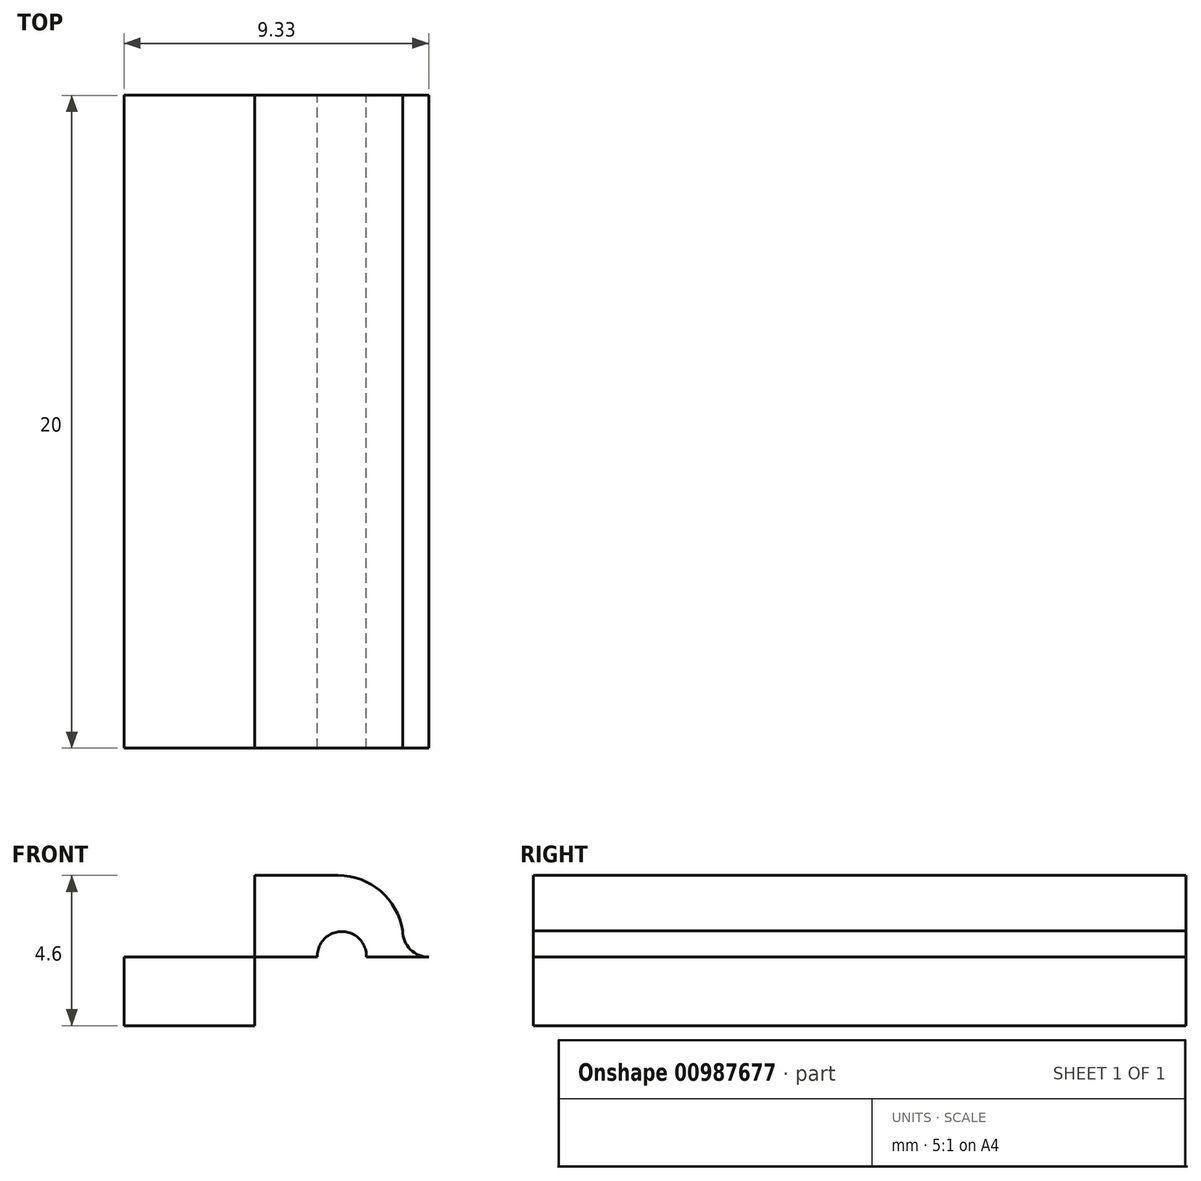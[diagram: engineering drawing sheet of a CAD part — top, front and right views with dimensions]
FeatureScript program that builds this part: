
annotation { "Feature Type Name" : "Feature", "Feature Type Description" : "" }
export const myFeature = defineFeature(function(context is Context, id is Id, definition is map)
    precondition{}
    {
        {
            var Q0;
            Q0=qCreatedBy(makeId("Top.planeOp"),FACE);
            var sketch = newSketch(context, id + "F0", { "sketchPlane" : qUnion([Q0])});
            skLineSegment(sketch, "E0", {"start": v(-65.72, -15.52) * mm, "end": v(10.28, -15.52) * mm});
            skLineSegment(sketch, "E1", {"start": v(-65.72, -15.52) * mm, "end": v(-65.72, 4.48) * mm});
            skLineSegment(sketch, "E2", {"start": v(-65.72, 4.48) * mm, "end": v(10.28, 4.48) * mm});
            skLineSegment(sketch, "E3", {"start": v(14.28, 0.48) * mm, "end": v(14.28, -11.52) * mm});
            skPoint(sketch, "E4.visualSharp", {"position": v(14.28, 4.48) * mm});
            skArc(sketch, "E4.filletArc", {"start": v(14.28, 0.48) * mm, "mid": v(13.1, 3.3) * mm, "end": v(10.28, 4.48) * mm});
            skPoint(sketch, "E5.visualSharp", {"position": v(14.28, -15.52) * mm});
            skArc(sketch, "E5.filletArc", {"start": v(10.28, -15.52) * mm, "mid": v(13.1, -14.35) * mm, "end": v(14.28, -11.52) * mm});
            skLineSegment(sketch, "E6", {"start": v(14.28, -5.52) * mm, "end": v(3.28, -5.52) * mm});
            skLineSegment(sketch, "E7", {"start": v(-65.72, 4.48) * mm, "end": v(-61.72, 4.48) * mm});
            skLineSegment(sketch, "E8", {"start": v(-61.72, 4.48) * mm, "end": v(-61.72, -15.52) * mm});
            skSolve(sketch);
        }
        {
            var Q0;
            Q0=makeQuery(id+"F0.imprint","IMPRINT",FACE,{"disambiguationData":[TD([[makeQuery(id+"F0.imprint","IMPRINT",EDGE,{"derivedFrom":sQuery(id+"F0.wireOp",EDGE,"E2")}),-1.0]])]});
            var Q1;
            Q1=makeQuery(id+"F0.imprint","IMPRINT",FACE,{"disambiguationData":[TD([[makeQuery(id+"F0.imprint","IMPRINT",EDGE,{"derivedFrom":sQuery(id+"F0.wireOp",EDGE,"6CRX7QyW-g7Fc-n8MB-8x00-72Ocf16J1GDi")}),-1.0]])]});
            extrude(context, id + "F1", {"entities" : qUnion([Q0, Q1]), "oppositeDirection" : true, "depth" : 2.1 * mm, "offsetDistance" : 25 * mm});
        }
        {
            var Q0;
            Q0=makeQuery(id+"F1.opExtrude","CAP_FACE",FACE,{"disambiguationData":[OSD([sQuery(id+"F0.wireOp",EDGE,"E0"),sQuery(id+"F0.wireOp",EDGE,"E2"),sQuery(id+"F0.wireOp",EDGE,"E3"),sQuery(id+"F0.wireOp",EDGE,"E4.filletArc"),sQuery(id+"F0.wireOp",EDGE,"E5.filletArc"),sQuery(id+"F0.wireOp",EDGE,"E8")])],"isStart":false});
            var sketch = newSketch(context, id + "F2", { "sketchPlane" : qUnion([Q0])});
            skLineSegment(sketch, "E9", {"start": v(14.28, 5.52) * mm, "end": v(3.28, 5.52) * mm});
            skCircle(sketch, "E10", {"center": v(3.28, 5.52) * mm, "radius": 1.5 * mm});
            skSolve(sketch);
        }
        {
            var Q0;
            Q0=makeQuery(id+"F2.imprint","IMPRINT",FACE,{"disambiguationData":[TD([[makeQuery(id+"F2.imprint","IMPRINT",EDGE,{"derivedFrom":sQuery(id+"F2.wireOp",EDGE,"E10")}),1.0]])]});
            extrude(context, id + "F3", {"entities" : qUnion([Q0]), "operationType" : NewBodyOperationType.REMOVE, "endBound" : BoundingType.THROUGH_ALL, "oppositeDirection" : true, "depth" : 25 * mm, "offsetDistance" : 25 * mm});
        }
        {
            var Q0;
            Q0=makeQuery(id+"F0.imprint","IMPRINT",FACE,{"disambiguationData":[TD([[makeQuery(id+"F0.imprint","IMPRINT",EDGE,{"derivedFrom":sQuery(id+"F0.wireOp",EDGE,"E2")}),-1.0]])]});
            var sketch = newSketch(context, id + "F4", { "sketchPlane" : qUnion([Q0])});
            skPoint(sketch, "E11", {"position": v(14.3, -5.52) * mm});
            skLineSegment(sketch, "E12", {"start": v(14.3, -5.52) * mm, "end": v(3.3, -5.52) * mm});
            skCircle(sketch, "E13", {"center": v(3.3, -5.52) * mm, "radius": 3.5 * mm});
            skSolve(sketch);
        }
        {
            var Q0;
            Q0=makeQuery(id+"F4.imprint","IMPRINT",FACE,{"disambiguationData":[TD([[makeQuery(id+"F4.imprint","IMPRINT",EDGE,{"derivedFrom":sQuery(id+"F4.wireOp",EDGE,"E13")}),1.0]])]});
            extrude(context, id + "F5", {"entities" : qUnion([Q0]), "operationType" : NewBodyOperationType.REMOVE, "oppositeDirection" : true, "depth" : 0.8 * mm, "offsetDistance" : 25 * mm});
        }
        {
            var Q0;
            Q0=makeQuery(id+"F1.opExtrude","CAP_FACE",FACE,{"disambiguationData":[OSD([sQuery(id+"F0.wireOp",EDGE,"E0"),sQuery(id+"F0.wireOp",EDGE,"E2"),sQuery(id+"F0.wireOp",EDGE,"E3"),sQuery(id+"F0.wireOp",EDGE,"E4.filletArc"),sQuery(id+"F0.wireOp",EDGE,"E5.filletArc"),sQuery(id+"F0.wireOp",EDGE,"E8")])],"isStart":false});
            var sketch = newSketch(context, id + "F6", { "sketchPlane" : qUnion([Q0])});
            skCircle(sketch, "E14", {"center": v(3.28, 5.52) * mm, "radius": 4.5 * mm});
            skSolve(sketch);
        }
        {
            var Q0;
            Q0=makeQuery(id+"F6.imprint","IMPRINT",FACE,{"disambiguationData":[TD([[makeQuery(id+"F6.imprint","IMPRINT",EDGE,{"derivedFrom":sQuery(id+"F6.wireOp",EDGE,"E14")}),1.0]])]});
            extrude(context, id + "F7", {"entities" : qUnion([Q0]), "operationType" : NewBodyOperationType.REMOVE, "oppositeDirection" : true, "depth" : 0.8 * mm, "offsetDistance" : 25 * mm});
        }
        {
            var Q0;
            Q0=makeQuery(id+"F1.opExtrude","SWEPT_FACE",FACE,{"disambiguationData":[OSD([sQuery(id+"F0.wireOp",EDGE,"E0")])]});
            var sketch = newSketch(context, id + "F8", { "sketchPlane" : qUnion([Q0])});
            skLineSegment(sketch, "E15.MirrorCS", {"start": v(-61.72, 2.5) * mm, "end": v(-59.17, 2.5) * mm});
            skArc(sketch, "E16.MirrorCS", {"start": v(-59.17, 2.5) * mm, "mid": v(-57.86, 2.02) * mm, "end": v(-57.19, 0.8) * mm});
            skArc(sketch, "E17.MirrorCS", {"start": v(-56.39, 0) * mm, "mid": v(-56.95, 0.23) * mm, "end": v(-57.19, 0.8) * mm});
            skLineSegment(sketch, "E18.MirrorCS", {"start": v(-57.19, 0) * mm, "end": v(-61.72, 0) * mm});
            skLineSegment(sketch, "E19", {"start": v(-61.72, 2.5) * mm, "end": v(-61.72, 0) * mm});
            skLineSegment(sketch, "E20", {"start": v(-56.39, 0) * mm, "end": v(-57.19, 0) * mm});
            skSolve(sketch);
        }
        {
            var Q0;
            Q0=makeQuery(id+"F8.imprint","IMPRINT",FACE,{"disambiguationData":[TD([[makeQuery(id+"F8.imprint","IMPRINT",EDGE,{"derivedFrom":sQuery(id+"F8.wireOp",EDGE,"E15.MirrorCS")}),-1.0]])]});
            extrude(context, id + "F9", {"entities" : qUnion([Q0]), "operationType" : NewBodyOperationType.ADD, "oppositeDirection" : true, "depth" : 20 * mm, "offsetDistance" : 25 * mm});
        }
        {
            var Q0;
            Q0=makeQuery(id+"F9.boolean.opBoolean","MERGE",FACE,{"derivedFrom":[makeQuery(id+"F1.opExtrude","SWEPT_FACE",FACE,{"disambiguationData":[OSD([sQuery(id+"F0.wireOp",EDGE,"E2")])]}),makeQuery(id+"F9.opExtrude","CAP_FACE",FACE,{"disambiguationData":[OSD([sQuery(id+"F8.wireOp",EDGE,"E15.MirrorCS"),sQuery(id+"F8.wireOp",EDGE,"E16.MirrorCS"),sQuery(id+"F8.wireOp",EDGE,"E17.MirrorCS"),sQuery(id+"F8.wireOp",EDGE,"E18.MirrorCS"),sQuery(id+"F8.wireOp",EDGE,"E19"),sQuery(id+"F8.wireOp",EDGE,"E20")])],"isStart":false})]});
            var sketch = newSketch(context, id + "F10", { "sketchPlane" : qUnion([Q0])});
            skCircle(sketch, "E21", {"center": v(59.05, 0.03) * mm, "radius": 0.75 * mm});
            skLineSegment(sketch, "E22", {"start": v(61.72, 2.5) * mm, "end": v(61.72, 0.03) * mm});
            skLineSegment(sketch, "E23", {"start": v(61.72, 0.03) * mm, "end": v(59.05, 0.03) * mm});
            skSolve(sketch);
        }
        {
            var Q0;
            Q0=makeQuery(id+"F10.imprint","IMPRINT",FACE,{"disambiguationData":[TD([[makeQuery(id+"F10.imprint","IMPRINT",EDGE,{"derivedFrom":sQuery(id+"F10.wireOp",EDGE,"E21")}),1.0]])]});
            extrude(context, id + "F11", {"entities" : qUnion([Q0]), "operationType" : NewBodyOperationType.REMOVE, "endBound" : BoundingType.THROUGH_ALL, "oppositeDirection" : true, "depth" : 25 * mm, "offsetDistance" : 25 * mm});
        }
    });
